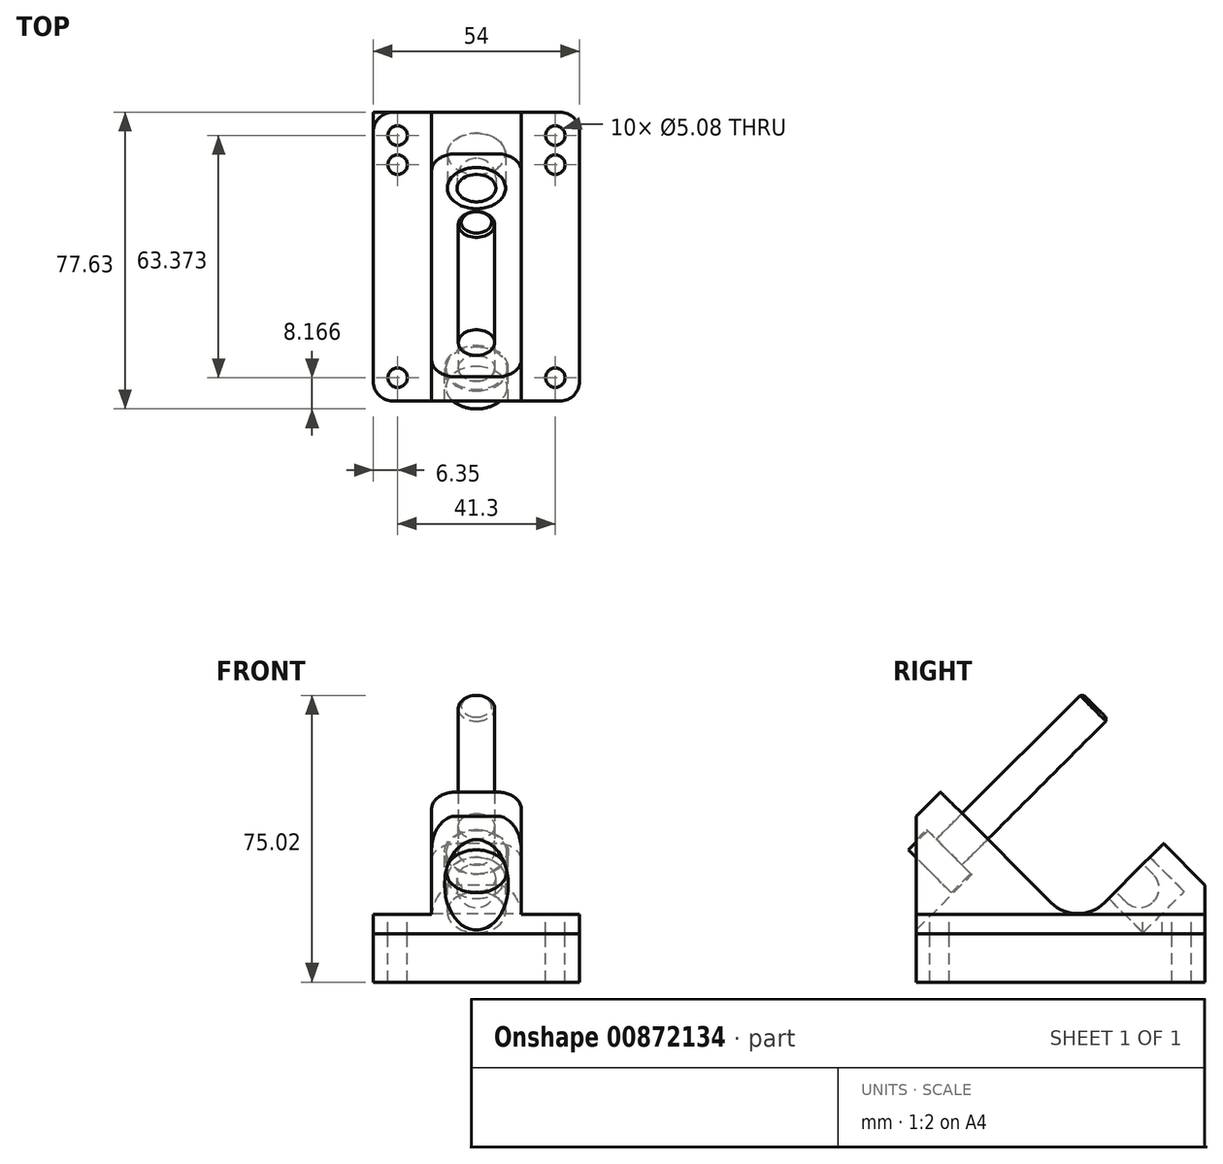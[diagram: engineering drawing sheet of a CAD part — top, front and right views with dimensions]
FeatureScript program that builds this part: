
annotation { "Feature Type Name" : "Feature", "Feature Type Description" : "" }
export const myFeature = defineFeature(function(context is Context, id is Id, definition is map)
    precondition{}
    {
        {
            var Q0;
            Q0=qCreatedBy(makeId("Right.planeOp"),FACE);
            var sketch = newSketch(context, id + "F0", { "sketchPlane" : qUnion([Q0])});
            skLineSegment(sketch, "E0", {"start": v(0, 0) * mm, "end": v(0, 30.72) * mm});
            skLineSegment(sketch, "E1", {"start": v(0, 30.72) * mm, "end": v(6.32, 37.04) * mm});
            skLineSegment(sketch, "E2", {"start": v(6.32, 37.04) * mm, "end": v(42.25, 1.12) * mm});
            skLineSegment(sketch, "E3", {"start": v(42.25, 1.12) * mm, "end": v(64.7, 23.57) * mm});
            skLineSegment(sketch, "E4", {"start": v(75.57, 12.7) * mm, "end": v(64.7, 23.57) * mm});
            skLineSegment(sketch, "E5", {"start": v(75.57, 12.7) * mm, "end": v(75.57, 0) * mm});
            skLineSegment(sketch, "E6", {"start": v(75.57, 0) * mm, "end": v(0, 0) * mm});
            skLineSegment(sketch, "E7", {"start": v(15.3, 28.06) * mm, "end": v(28.77, 41.53) * mm, "construction": true});
            skLineSegment(sketch, "E8", {"start": v(28.77, 41.53) * mm, "end": v(64.7, 5.6) * mm, "construction": true});
            skLineSegment(sketch, "E9", {"start": v(64.7, 5.6) * mm, "end": v(70.08, 11) * mm, "construction": true});
            skLineSegment(sketch, "E10", {"start": v(70.08, 11) * mm, "end": v(61.1, 19.98) * mm, "construction": true});
            skLineSegment(sketch, "E11", {"start": v(28.77, 41.53) * mm, "end": v(15.3, 55) * mm, "construction": true});
            skCircle(sketch, "E12", {"center": v(15.3, 55) * mm, "radius": 4 * mm, "construction": true});
            skLineSegment(sketch, "E13", {"start": v(64.7, 5.6) * mm, "end": v(59.3, 0.22) * mm, "construction": true});
            skLineSegment(sketch, "E14", {"start": v(59.3, 0.22) * mm, "end": v(50.33, 9.2) * mm, "construction": true});
            skCircle(sketch, "E15", {"center": v(58.4, 11.9) * mm, "radius": 5.08 * mm, "construction": true});
            skSolve(sketch);
        }
        {
            var Q0;
            Q0 = qSketchRegion(id + "F0", true);
            var Q1;
            Q1 = qConstructionFilter(qBodyType(qCreatedBy(id + "F0" ,EDGE), BodyType.WIRE), ConstructionObject.NO);
            extrude(context, id + "F1", {"entities" : qUnion([Q0]), "surfaceEntities" : qUnion([Q1]), "depth" : 27 * mm, "offsetDistance" : 25.4 * mm});
        }
        {
            var Q0;
            Q0=makeQuery(id+"F1.opExtrude","SWEPT_EDGE",EDGE,{"disambiguationData":[OSD([sQuery(id+"F0.wireOp",EDGE,"E2"),sQuery(id+"F0.wireOp",EDGE,"E3")])]});
            fillet(context, id + "F2", {"entities" : qUnion([Q0]), "radius" : 9.9 * mm, "tangentPropagation" : true, "allowEdgeOverflow" : false});
        }
        {
            var Q0;
            Q0=makeQuery(id+"F1.opExtrude","CAP_FACE",FACE,{"disambiguationData":[OSD([sQuery(id+"F0.wireOp",EDGE,"E0"),sQuery(id+"F0.wireOp",EDGE,"E1"),sQuery(id+"F0.wireOp",EDGE,"E2"),sQuery(id+"F0.wireOp",EDGE,"E3"),sQuery(id+"F0.wireOp",EDGE,"E4"),sQuery(id+"F0.wireOp",EDGE,"E5"),sQuery(id+"F0.wireOp",EDGE,"E6")])],"isStart":false});
            var sketch = newSketch(context, id + "F3", { "sketchPlane" : qUnion([Q0])});
            skLineSegment(sketch, "E16.bottom", {"start": v(0, 37.04) * mm, "end": v(75.57, 37.04) * mm});
            skLineSegment(sketch, "E16.top", {"start": v(0, 5.08) * mm, "end": v(75.57, 5.08) * mm});
            skLineSegment(sketch, "E16.left", {"start": v(0, 37.04) * mm, "end": v(0, 5.08) * mm});
            skLineSegment(sketch, "E16.right", {"start": v(75.57, 37.04) * mm, "end": v(75.57, 5.08) * mm});
            skSolve(sketch);
        }
        {
            var Q0;
            Q0 = qSketchRegion(id + "F3", true);
            extrude(context, id + "F4", {"entities" : qUnion([Q0]), "operationType" : NewBodyOperationType.REMOVE, "oppositeDirection" : true, "depth" : 15.24 * mm, "offsetDistance" : 25.4 * mm});
        }
        {
            var Q0;
            Q0=makeQuery(id+"F4.boolean.opBoolean","COPY",FACE,{"derivedFrom":makeQuery(id+"F4.opExtrude","SWEPT_FACE",FACE,{"disambiguationData":[OSD([sQuery(id+"F3.wireOp",EDGE,"E16.top")])]})});
            var sketch = newSketch(context, id + "F5", { "sketchPlane" : qUnion([Q0])});
            skLineSegment(sketch, "E17", {"start": v(20.65, 69.47) * mm, "end": v(20.65, 61.85) * mm, "construction": true});
            skLineSegment(sketch, "E18", {"start": v(20.65, 61.85) * mm, "end": v(20.65, 6.1) * mm, "construction": true});
            skCircle(sketch, "E19", {"center": v(20.65, 69.47) * mm, "radius": 2.54 * mm});
            skCircle(sketch, "E20", {"center": v(20.65, 61.85) * mm, "radius": 2.54 * mm});
            skCircle(sketch, "E21", {"center": v(20.65, 6.1) * mm, "radius": 2.54 * mm});
            skSolve(sketch);
        }
        {
            var Q0;
            Q0=makeQuery(id+"F4.boolean.opBoolean","INTERSECT",EDGE,{"derivedFrom":[makeQuery(id+"F1.opExtrude","SWEPT_FACE",FACE,{"disambiguationData":[OSD([sQuery(id+"F0.wireOp",EDGE,"E1")])]}),makeQuery(id+"F4.opExtrude","CAP_FACE",FACE,{"disambiguationData":[OSD([sQuery(id+"F3.wireOp",EDGE,"E16.bottom"),sQuery(id+"F3.wireOp",EDGE,"E16.top"),sQuery(id+"F3.wireOp",EDGE,"E16.left"),sQuery(id+"F3.wireOp",EDGE,"E16.right")])],"isStart":false})]});
            var Q1;
            Q1=makeQuery(id+"F4.boolean.opBoolean","INTERSECT",EDGE,{"derivedFrom":[makeQuery(id+"F1.opExtrude","SWEPT_FACE",FACE,{"disambiguationData":[OSD([sQuery(id+"F0.wireOp",EDGE,"E4")])]}),makeQuery(id+"F4.opExtrude","CAP_FACE",FACE,{"disambiguationData":[OSD([sQuery(id+"F3.wireOp",EDGE,"E16.bottom"),sQuery(id+"F3.wireOp",EDGE,"E16.top"),sQuery(id+"F3.wireOp",EDGE,"E16.left"),sQuery(id+"F3.wireOp",EDGE,"E16.right")])],"isStart":false})]});
            fillet(context, id + "F6", {"entities" : qUnion([Q0, Q1]), "radius" : 6.35 * mm, "tangentPropagation" : true, "allowEdgeOverflow" : false});
        }
        {
            var Q0;
            Q0=makeQuery(id+"F1.opExtrude","CAP_EDGE",EDGE,{"disambiguationData":[OSD([sQuery(id+"F0.wireOp",EDGE,"E0")])],"isStart":false});
            var Q1;
            Q1=makeQuery(id+"F1.opExtrude","CAP_EDGE",EDGE,{"disambiguationData":[OSD([sQuery(id+"F0.wireOp",EDGE,"E5")])],"isStart":false});
            fillet(context, id + "F7", {"entities" : qUnion([Q0, Q1]), "radius" : 5.08 * mm, "tangentPropagation" : true, "allowEdgeOverflow" : false});
        }
        {
            var Q0;
            Q0 = qSketchRegion(id + "F5", true);
            extrude(context, id + "F8", {"entities" : qUnion([Q0]), "operationType" : NewBodyOperationType.REMOVE, "endBound" : BoundingType.THROUGH_ALL, "oppositeDirection" : true, "depth" : 25.4 * mm, "offsetDistance" : 25.4 * mm});
        }
        {
            var Q0;
            Q0=makeQuery(id+"F1.opExtrude","SWEPT_BODY",BODY,{"disambiguationData":[OSD([sQuery(id+"F0.wireOp",EDGE,"E0"),sQuery(id+"F0.wireOp",EDGE,"E1"),sQuery(id+"F0.wireOp",EDGE,"E2"),sQuery(id+"F0.wireOp",EDGE,"E3"),sQuery(id+"F0.wireOp",EDGE,"E4"),sQuery(id+"F0.wireOp",EDGE,"E5"),sQuery(id+"F0.wireOp",EDGE,"E6")])]});
            var Q1;
            Q1=makeQuery(id+"F1.opExtrude","CAP_FACE",FACE,{"disambiguationData":[OSD([sQuery(id+"F0.wireOp",EDGE,"E0"),sQuery(id+"F0.wireOp",EDGE,"E1"),sQuery(id+"F0.wireOp",EDGE,"E2"),sQuery(id+"F0.wireOp",EDGE,"E3"),sQuery(id+"F0.wireOp",EDGE,"E4"),sQuery(id+"F0.wireOp",EDGE,"E5"),sQuery(id+"F0.wireOp",EDGE,"E6")])],"isStart":true});
            mirror(context, id + "F9", {"operationType" : NewBodyOperationType.ADD, "entities" : qUnion([Q0]), "mirrorPlane" : qUnion([Q1])});
        }
        {
            var Q0;
            Q0=qCreatedBy(makeId("Right.planeOp"),FACE);
            var sketch = newSketch(context, id + "F10", { "sketchPlane" : qUnion([Q0])});
            skLineSegment(sketch, "E22.0", {"start": v(15.3, 28.06) * mm, "end": v(28.77, 41.53) * mm, "construction": true});
            skLineSegment(sketch, "E22.1", {"start": v(6.32, 37.04) * mm, "end": v(42.25, 1.12) * mm, "construction": true});
            skLineSegment(sketch, "E23", {"start": v(15.3, 28.06) * mm, "end": v(11.94, 31.43) * mm});
            skLineSegment(sketch, "E24", {"start": v(11.94, 31.43) * mm, "end": v(5.2, 24.7) * mm});
            skLineSegment(sketch, "E25", {"start": v(5.2, 24.7) * mm, "end": v(2.67, 27.22) * mm});
            skLineSegment(sketch, "E26", {"start": v(2.67, 27.22) * mm, "end": v(-12.28, 12.28) * mm});
            skLineSegment(sketch, "E27", {"start": v(-12.28, 12.28) * mm, "end": v(-6.38, 6.38) * mm});
            skLineSegment(sketch, "E28", {"start": v(-6.38, 6.38) * mm, "end": v(15.3, 28.06) * mm});
            skLineSegment(sketch, "E29", {"start": v(-6.38, 6.38) * mm, "end": v(0, 0) * mm, "construction": true});
            skSolve(sketch);
        }
        {
            var Q0;
            Q0 = qSketchRegion(id + "F10", true);
            var Q1;
            Q1=sQuery(id+"F10.wireOp",EDGE,"E22.0");
            revolve(context, id + "F11", {"operationType" : NewBodyOperationType.REMOVE, "surfaceOperationType" : NewSurfaceOperationType.NEW, "entities" : qUnion([Q0]), "axis" : qUnion([Q1]), "revolveType" : RevolveType.FULL, "oppositeDirection" : true});
        }
        {
            var Q0;
            Q0=qCreatedBy(makeId("Right.planeOp"),FACE);
            var sketch = newSketch(context, id + "F12", { "sketchPlane" : qUnion([Q0])});
            skLineSegment(sketch, "E30.1", {"start": v(5.2, 24.7) * mm, "end": v(2.96, 26.94) * mm});
            skLineSegment(sketch, "E30.2", {"start": v(11.94, 31.43) * mm, "end": v(5.2, 24.7) * mm});
            skLineSegment(sketch, "E31", {"start": v(2.96, 26.94) * mm, "end": v(-2.07, 21.9) * mm});
            skPoint(sketch, "E30.0.end.orphan", {"position": v(-12.28, 12.28) * mm});
            skPoint(sketch, "E32.orphan", {"position": v(2.67, 27.22) * mm});
            skLineSegment(sketch, "E33", {"start": v(-2.07, 21.9) * mm, "end": v(3.53, 16.29) * mm});
            skLineSegment(sketch, "E34.0", {"start": v(15.3, 28.06) * mm, "end": v(28.77, 41.53) * mm, "construction": true});
            skLineSegment(sketch, "E35", {"start": v(3.53, 16.29) * mm, "end": v(46.74, 59.5) * mm});
            skLineSegment(sketch, "E36", {"start": v(46.74, 59.5) * mm, "end": v(43.37, 62.86) * mm});
            skLineSegment(sketch, "E37", {"start": v(43.37, 62.86) * mm, "end": v(5.2, 24.68) * mm});
            skSolve(sketch);
        }
        {
            var Q0;
            Q0 = qSketchRegion(id + "F12", true);
            var Q1;
            Q1=sQuery(id+"F12.wireOp",EDGE,"E35");
            revolve(context, id + "F13", {"surfaceOperationType" : NewSurfaceOperationType.NEW, "entities" : qUnion([Q0]), "axis" : qUnion([Q1]), "revolveType" : RevolveType.FULL});
        }
        {
            var Q0;
            Q0=makeQuery(id+"F13.opRevolve","SWEPT_EDGE",EDGE,{"disambiguationData":[OSD([sQuery(id+"F12.wireOp",EDGE,"E36"),sQuery(id+"F12.wireOp",EDGE,"E37")])]});
            chamfer(context, id + "F14", {"entities" : qUnion([Q0]), "width" : 0.76 * mm, "tangentPropagation" : true});
        }
        {
            var Q0;
            Q0=qCreatedBy(makeId("Right.planeOp"),FACE);
            var sketch = newSketch(context, id + "F15", { "sketchPlane" : qUnion([Q0])});
            skLineSegment(sketch, "E38.0", {"start": v(70.08, 11) * mm, "end": v(61.1, 19.98) * mm});
            skLineSegment(sketch, "E39.0", {"start": v(64.7, 5.6) * mm, "end": v(70.08, 11) * mm});
            skLineSegment(sketch, "E40.0", {"start": v(28.77, 41.53) * mm, "end": v(64.7, 5.6) * mm});
            skLineSegment(sketch, "E41.0", {"start": v(55.72, 14.59) * mm, "end": v(61.1, 19.98) * mm});
            skPoint(sketch, "E42.orphan", {"position": v(64.7, 23.57) * mm});
            skPoint(sketch, "E43.orphan", {"position": v(42.25, 1.12) * mm});
            skSolve(sketch);
        }
        {
            var Q0;
            Q0 = qSketchRegion(id + "F15", true);
            var Q1;
            Q1=sQuery(id+"F15.wireOp",EDGE,"E40.0");
            revolve(context, id + "F16", {"operationType" : NewBodyOperationType.REMOVE, "surfaceOperationType" : NewSurfaceOperationType.NEW, "entities" : qUnion([Q0]), "axis" : qUnion([Q1]), "revolveType" : RevolveType.FULL, "oppositeDirection" : true});
        }
        {
            var Q0;
            Q0=qCreatedBy(makeId("Right.planeOp"),FACE);
            var sketch = newSketch(context, id + "F17", { "sketchPlane" : qUnion([Q0])});
            skArc(sketch, "E44.0", {"start": v(62, 8.3) * mm, "mid": v(63.49, 11.9) * mm, "end": v(62, 15.49) * mm});
            skLineSegment(sketch, "E45.0", {"start": v(59.3, 18.18) * mm, "end": v(61.1, 19.98) * mm});
            skLineSegment(sketch, "E46.0", {"start": v(70.08, 11) * mm, "end": v(61.1, 19.98) * mm});
            skLineSegment(sketch, "E47.0", {"start": v(64.7, 5.6) * mm, "end": v(70.08, 11) * mm});
            skLineSegment(sketch, "E48.trimOffspring", {"start": v(62, 8.3) * mm, "end": v(64.7, 5.6) * mm});
            skLineSegment(sketch, "E49", {"start": v(59.3, 18.18) * mm, "end": v(62, 15.49) * mm});
            skSolve(sketch);
        }
        {
            var Q0;
            Q0 = qSketchRegion(id + "F17", true);
            var Q1;
            Q1=sQuery(id+"F17.wireOp",EDGE,"E48.trimOffspring");
            revolve(context, id + "F18", {"surfaceOperationType" : NewSurfaceOperationType.NEW, "entities" : qUnion([Q0]), "axis" : qUnion([Q1]), "revolveType" : RevolveType.FULL});
        }
        {
            var Q0;
            {var subQ0=makeQuery(id+"F1.opExtrude","SWEPT_FACE",FACE,{"disambiguationData":[OSD([sQuery(id+"F0.wireOp",EDGE,"E6")])]});Q0=makeQuery(id+"F9.boolean.opBoolean","MERGE",FACE,{"derivedFrom":[subQ0,makeQuery(id+"F9.opPattern","COPY",FACE,{"derivedFrom":subQ0,"instanceName":"1"})]});}
            var sketch = newSketch(context, id + "F19", { "sketchPlane" : qUnion([Q0])});
            skLineSegment(sketch, "E50.0", {"start": v(-27, -75.57) * mm, "end": v(-27, 0) * mm});
            skLineSegment(sketch, "E51.0", {"start": v(27, 0) * mm, "end": v(-27, 0) * mm});
            skLineSegment(sketch, "E52.0", {"start": v(27, -75.57) * mm, "end": v(27, 0) * mm});
            skLineSegment(sketch, "E53.0", {"start": v(27, -75.57) * mm, "end": v(-27, -75.57) * mm});
            skLineSegment(sketch, "E54.0.1", {"start": v(-27, 0) * mm, "end": v(-27, -75.57) * mm});
            skLineSegment(sketch, "E54.0.2", {"start": v(-27, -75.57) * mm, "end": v(27, -75.57) * mm});
            skCircle(sketch, "E55.0", {"center": v(-20.65, -69.47) * mm, "radius": 2.54 * mm});
            skCircle(sketch, "E56.0", {"center": v(-20.65, -6.1) * mm, "radius": 2.54 * mm});
            skCircle(sketch, "E57.0", {"center": v(20.65, -6.1) * mm, "radius": 2.54 * mm});
            skCircle(sketch, "E58.0", {"center": v(20.65, -69.47) * mm, "radius": 2.54 * mm});
            skSolve(sketch);
        }
        {
            var Q0;
            Q0 = qSketchRegion(id + "F19", true);
            extrude(context, id + "F20", {"entities" : qUnion([Q0]), "depth" : 12.7 * mm, "offsetDistance" : 25.4 * mm});
        }
        {
            var Q0;
            Q0=makeQuery(id+"F20.opExtrude","SWEPT_EDGE",EDGE,{"disambiguationData":[OSD([sQuery(id+"F19.wireOp",EDGE,"E51.0"),sQuery(id+"F19.wireOp",EDGE,"E52.0")])]});
            var Q1;
            Q1=makeQuery(id+"F20.opExtrude","SWEPT_EDGE",EDGE,{"disambiguationData":[OSD([sQuery(id+"F19.wireOp",EDGE,"E54.0.2"),sQuery(id+"F19.wireOp",EDGE,"E52.0")])]});
            var Q2;
            Q2=makeQuery(id+"F20.opExtrude","SWEPT_EDGE",EDGE,{"disambiguationData":[OSD([sQuery(id+"F19.wireOp",EDGE,"E51.0"),sQuery(id+"F19.wireOp",EDGE,"E54.0.1")])]});
            var Q3;
            Q3=makeQuery(id+"F20.opExtrude","SWEPT_EDGE",EDGE,{"disambiguationData":[OSD([sQuery(id+"F19.wireOp",EDGE,"E54.0.1"),sQuery(id+"F19.wireOp",EDGE,"E54.0.2")])]});
            fillet(context, id + "F21", {"entities" : qUnion([Q0, Q1, Q2, Q3]), "radius" : 5.08 * mm, "tangentPropagation" : true, "allowEdgeOverflow" : false});
        }
    });
